# Revit family: MC_Puerta Batiente 2 Hoja
name_source: partatom
category: Doors
revit_build: Autodesk Revit 2017 (Build: 20190508_0315(x64)
units: mm (PartAtom-declared; Revit-internal decimal feet)

## family parameters
Always vertical = Yes
Cut with Voids When Loaded = No
OmniClass Number = 23.30.10.00
OmniClass Title = Doors
Room Calculation Point = No
Shared = No

## types (1)
- MC_Puerta Batiente 2 Hoja
    Analytic Construction = <None>
    Ancho Bastidor = 100 mm  [stored 0.328084 ft]
    Bastidor = Stainless Steel AISI 304
    Description = Batiente 2 Hojas
    Function = Exterior
    Manufacturer = G-U
    Model = Batiente 2 Hojas
    Perfil Brazo Extensor = Stainless Steel AISI 304
    Sensor = Stainless Steel AISI 304
    Thickness = 40 mm  [stored 0.131234 ft]
    Tipo = Batiente
    URL = http://www.automatics.cl
    Vidrio = Glass

note: [stored X ft] marks values corroborated as IEEE doubles in the binary element streams (Revit-internal decimal feet)

## geometry (parser evidence)
native form markers: Sweep x6
no freeform markers — native parametric forms only
